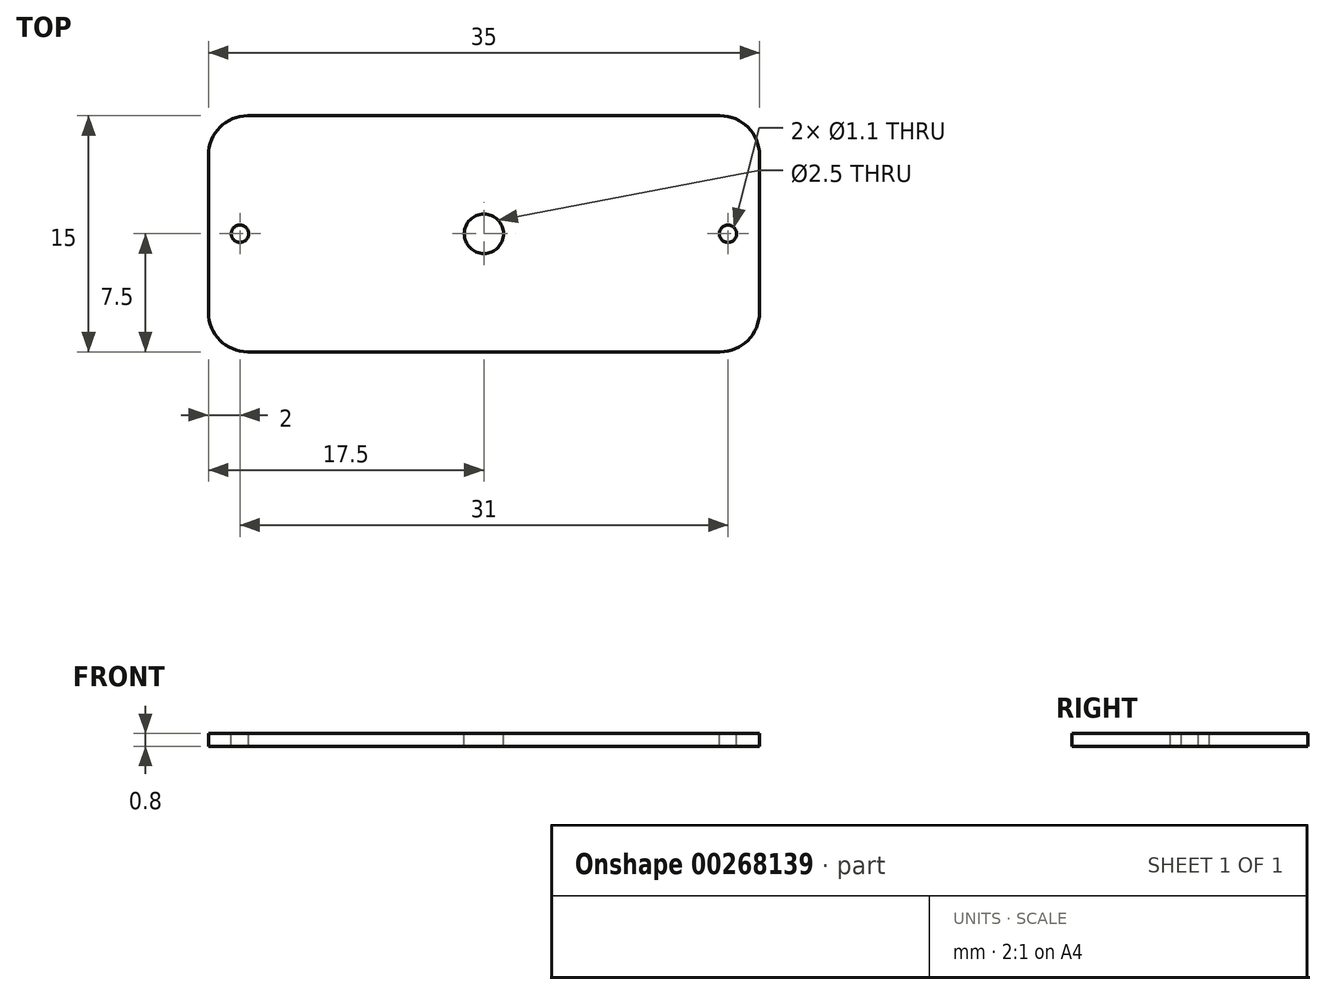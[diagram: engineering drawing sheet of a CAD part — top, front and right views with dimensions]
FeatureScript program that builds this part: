
annotation { "Feature Type Name" : "Feature", "Feature Type Description" : "" }
export const myFeature = defineFeature(function(context is Context, id is Id, definition is map)
    precondition{}
    {
        {
            var Q0;
            Q0=qCreatedBy(makeId("Top.planeOp"),FACE);
            var sketch = newSketch(context, id + "F0", { "sketchPlane" : qUnion([Q0])});
            skLineSegment(sketch, "E0.bottom", {"start": v(-15, 7.5) * mm, "end": v(15, 7.5) * mm});
            skLineSegment(sketch, "E0.top", {"start": v(-15, -7.5) * mm, "end": v(15, -7.5) * mm});
            skLineSegment(sketch, "E0.left", {"start": v(-17.5, 5) * mm, "end": v(-17.5, -5) * mm});
            skLineSegment(sketch, "E0.right", {"start": v(17.5, 5) * mm, "end": v(17.5, -5) * mm});
            skPoint(sketch, "E0.middle", {"position": v(0, 0) * mm});
            skPoint(sketch, "E1.visualSharp", {"position": v(-17.5, 7.5) * mm});
            skArc(sketch, "E1.filletArc", {"start": v(-15, 7.5) * mm, "mid": v(-16.77, 6.77) * mm, "end": v(-17.5, 5) * mm});
            skPoint(sketch, "E2.visualSharp", {"position": v(17.5, 7.5) * mm});
            skArc(sketch, "E2.filletArc", {"start": v(17.5, 5) * mm, "mid": v(16.77, 6.77) * mm, "end": v(15, 7.5) * mm});
            skPoint(sketch, "E3.visualSharp", {"position": v(17.5, -7.5) * mm});
            skArc(sketch, "E3.filletArc", {"start": v(15, -7.5) * mm, "mid": v(16.77, -6.77) * mm, "end": v(17.5, -5) * mm});
            skPoint(sketch, "E4.visualSharp", {"position": v(-17.5, -7.5) * mm});
            skArc(sketch, "E4.filletArc", {"start": v(-17.5, -5) * mm, "mid": v(-16.77, -6.77) * mm, "end": v(-15, -7.5) * mm});
            skSolve(sketch);
        }
        {
            var Q0;
            Q0 = qSketchRegion(id + "F0", true);
            extrude(context, id + "F1", {"entities" : qUnion([Q0]), "depth" : 0.8 * mm, "offsetDistance" : 25 * mm});
        }
        {
            var Q0;
            Q0=makeQuery(id+"F1.opExtrude","CAP_FACE",FACE,{"disambiguationData":[OSD([sQuery(id+"F0.wireOp",EDGE,"E0.bottom"),sQuery(id+"F0.wireOp",EDGE,"E0.top"),sQuery(id+"F0.wireOp",EDGE,"E0.left"),sQuery(id+"F0.wireOp",EDGE,"E0.right")])],"isStart":false});
            var sketch = newSketch(context, id + "F2", { "sketchPlane" : qUnion([Q0])});
            skCircle(sketch, "E5", {"center": v(0, 0) * mm, "radius": 1.25 * mm});
            skLineSegment(sketch, "E6", {"start": v(0, 0) * mm, "end": v(-10, 0) * mm});
            skLineSegment(sketch, "E7", {"start": v(-10, 0) * mm, "end": v(-15.5, 0) * mm});
            skCircle(sketch, "E8", {"center": v(-15.5, 0) * mm, "radius": 0.55 * mm});
            skLineSegment(sketch, "E9", {"start": v(0, 0) * mm, "end": v(10, 0) * mm});
            skLineSegment(sketch, "E10", {"start": v(10, 0) * mm, "end": v(15.5, 0) * mm});
            skCircle(sketch, "E11", {"center": v(15.5, 0) * mm, "radius": 0.55 * mm});
            skSolve(sketch);
        }
        {
            var Q0;
            Q0=makeQuery(id+"F2.imprint","IMPRINT",FACE,{"disambiguationData":[TD([[makeQuery(id+"F2.imprint","IMPRINT",EDGE,{"derivedFrom":sQuery(id+"F2.wireOp",EDGE,"E5")}),1.0]])]});
            var Q1;
            Q1=makeQuery(id+"F2.imprint","IMPRINT",FACE,{"disambiguationData":[TD([[makeQuery(id+"F2.imprint","IMPRINT",EDGE,{"derivedFrom":sQuery(id+"F2.wireOp",EDGE,"E8")}),1.0]])]});
            var Q2;
            Q2=makeQuery(id+"F2.imprint","IMPRINT",FACE,{"disambiguationData":[TD([[makeQuery(id+"F2.imprint","IMPRINT",EDGE,{"derivedFrom":sQuery(id+"F2.wireOp",EDGE,"E11")}),1.0]])]});
            extrude(context, id + "F3", {"entities" : qUnion([Q0, Q1, Q2]), "operationType" : NewBodyOperationType.REMOVE, "endBound" : BoundingType.THROUGH_ALL, "oppositeDirection" : true, "depth" : 25 * mm, "offsetDistance" : 25 * mm});
        }
    });
